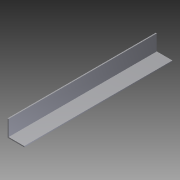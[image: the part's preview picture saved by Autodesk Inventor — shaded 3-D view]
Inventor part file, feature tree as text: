
AUTODESK INVENTOR PART (.ipt)
format: ipt  version: 2012 (Build 160160000, 160)  size: 81,408 bytes
history: native  units: in
note: dims shown in document units (in); Inventor stores cm internally (conversion verified against a paired STEP export)
features: other x3, sketch x2
ambient origin geometry x8: Origin, YZ Plane, XZ Plane, XY Plane, X Axis, Y Axis, Z Axis, Center Point
bodies: Solid1 (feature_tree)
feature tree (5):
  other  "8 ball top lift point.ipt"
  other  "Solid1::8 ball top lift point.ipt"
  sketch  "Sketch1"  dims[d0=0.3937in]
  sketch  "Sketch2"
  other  "TaggingFeature1"
